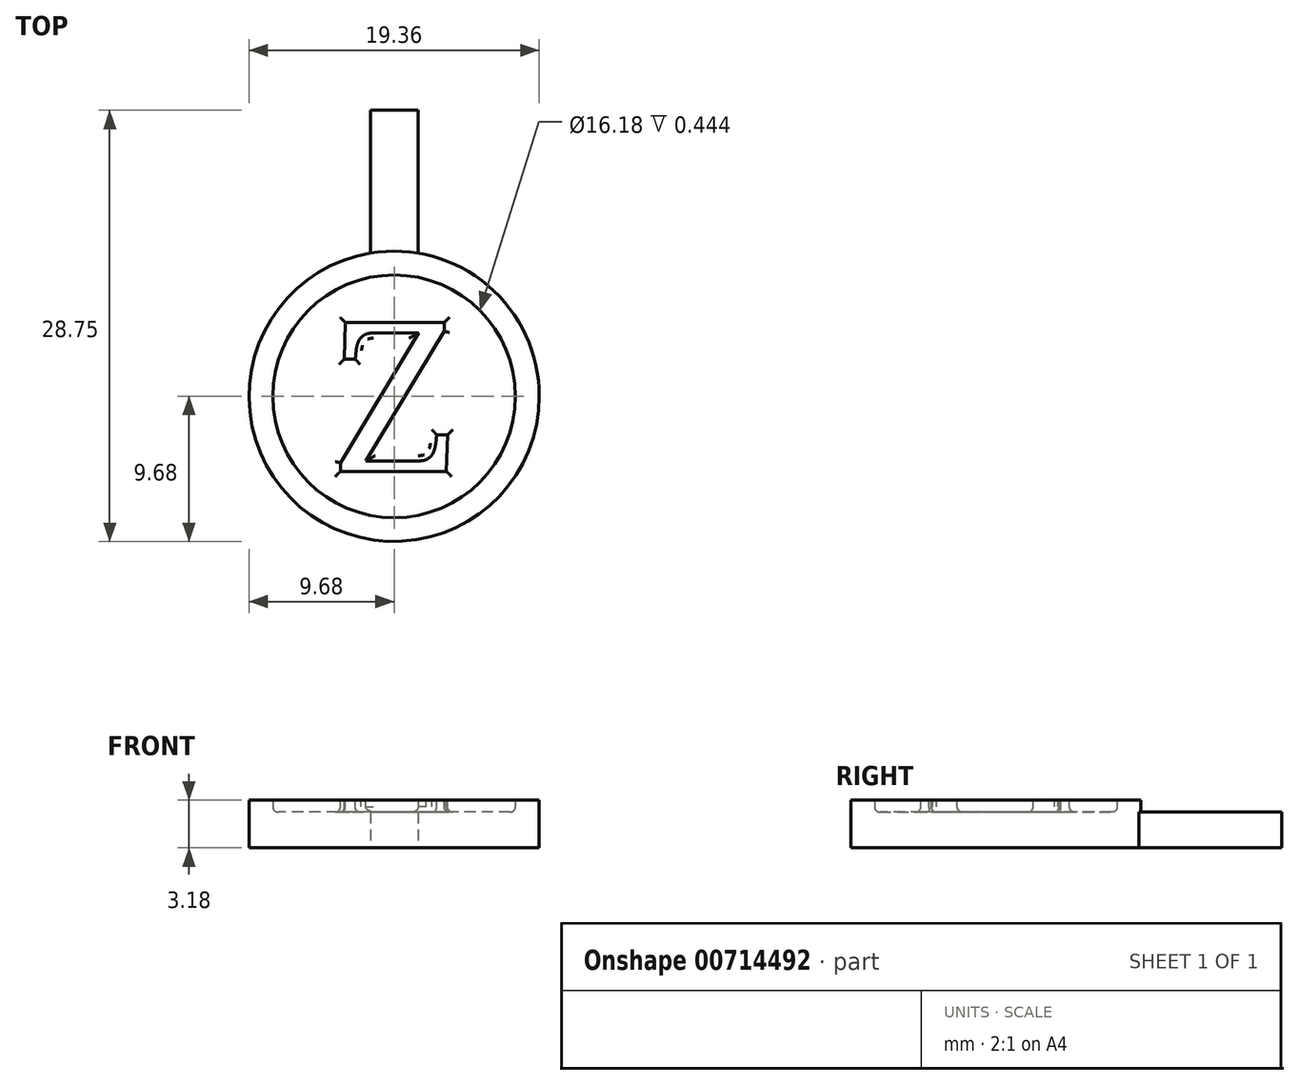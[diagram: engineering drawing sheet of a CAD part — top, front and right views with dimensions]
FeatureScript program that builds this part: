
annotation { "Feature Type Name" : "Feature", "Feature Type Description" : "" }
export const myFeature = defineFeature(function(context is Context, id is Id, definition is map)
    precondition{}
    {
        {
            var Q0;
            Q0=qCreatedBy(makeId("Top.planeOp"),FACE);
            var sketch = newSketch(context, id + "F0", { "sketchPlane" : qUnion([Q0])});
            skCircle(sketch, "E0", {"center": v(0, 0) * mm, "radius": 9.68 * mm});
            skSolve(sketch);
        }
        {
            var Q0;
            Q0=qSketchRegion(id+"F0",true);
            extrude(context, id + "F1", {"entities" : qUnion([Q0]), "depth" : 2.38 * mm, "offsetDistance" : 25.4 * mm});
        }
        {
            var Q0;
            Q0=makeQuery(id+"F1.opExtrude","CAP_FACE",FACE,{"disambiguationData":[OSD([sQuery(id+"F0.wireOp",EDGE,"E0")])],"isStart":false});
            var sketch = newSketch(context, id + "F2", { "sketchPlane" : qUnion([Q0])});
            skCircle(sketch, "E1.0.0", {"center": v(0, 0) * mm, "radius": 9.68 * mm});
            skCircle(sketch, "E2.0", {"center": v(0, 0) * mm, "radius": 8.09 * mm});
            skSolve(sketch);
        }
        {
            var Q0;
            Q0=makeQuery(id+"F2.imprint","IMPRINT",FACE,{"disambiguationData":[TD([[makeQuery(id+"F2.imprint","IMPRINT",EDGE,{"derivedFrom":sQuery(id+"F2.wireOp",EDGE,"E1.0.0")}),1.0]])]});
            extrude(context, id + "F3", {"entities" : qUnion([Q0]), "operationType" : NewBodyOperationType.ADD, "depth" : 0.8 * mm, "offsetDistance" : 25.4 * mm});
        }
        {
            var Q0;
            Q0=qCreatedBy(makeId("Top.planeOp"),FACE);
            var sketch = newSketch(context, id + "F4", { "sketchPlane" : qUnion([Q0])});
            skLineSegment(sketch, "E3.bottom", {"start": v(1.59, 9.55) * mm, "end": v(-1.59, 9.55) * mm});
            skLineSegment(sketch, "E3.top", {"start": v(1.59, 19.07) * mm, "end": v(-1.59, 19.07) * mm});
            skLineSegment(sketch, "E3.left", {"start": v(1.59, 9.55) * mm, "end": v(1.59, 19.07) * mm});
            skLineSegment(sketch, "E3.right", {"start": v(-1.59, 9.55) * mm, "end": v(-1.59, 19.07) * mm});
            skPoint(sketch, "E3.middle", {"position": v(0, 14.3) * mm});
            skSolve(sketch);
        }
        {
            var Q0;
            Q0=qSketchRegion(id+"F4",true);
            var Q1;
            Q1=makeQuery(id+"F3.opExtrude","CAP_FACE",FACE,{"disambiguationData":[OSD([sQuery(id+"F2.wireOp",EDGE,"E1.0.0"),sQuery(id+"F2.wireOp",EDGE,"E2.0")])],"isStart":false});
            extrude(context, id + "F5", {"entities" : qUnion([Q0]), "operationType" : NewBodyOperationType.ADD, "depth" : 2.38 * mm, "endBoundEntityFace" : qUnion([Q1]), "hasOffset" : true, "offsetDistance" : 1 * mm});
        }
        {
            var Q0;
            Q0=makeQuery(id+"F3.opExtrude","CAP_FACE",FACE,{"disambiguationData":[OSD([sQuery(id+"F2.wireOp",EDGE,"E1.0.0"),sQuery(id+"F2.wireOp",EDGE,"E2.0")])],"isStart":false});
            var sketch = newSketch(context, id + "F6", { "sketchPlane" : qUnion([Q0])});
            skPoint(sketch, "E4.middle", {"position": v(0, 0) * mm});
            skText(sketch, "E5", { "text": "Z", "fontName": "NotoSerif-Regular.ttf"});
            skLineSegment(sketch, "E6", {"start": v(4.46, 0) * mm, "end": v(-4.08, 0) * mm, "construction": true});
            skLineSegment(sketch, "E7", {"start": v(0, 8.09) * mm, "end": v(0, -8.09) * mm, "construction": true});
            skLineSegment(sketch, "E8", {"start": v(-8.09, 0) * mm, "end": v(8.09, 0) * mm, "construction": true});
            const initialGuessF6  = {"E5": [-0.00408, -0.005, 1, 0, 0.01]};
            skSetInitialGuess(sketch, initialGuessF6);
            skSolve(sketch);
        }
        {
            var Q0;
            Q0=makeQuery(id+"F6.imprint","IMPRINT",FACE,{"disambiguationData":[TD([[makeQuery(id+"F6.imprint","IMPRINT",EDGE,{"derivedFrom":sQuery(id+"F6.wireOp",EDGE,"E5.sketch_text.stroke-0")}),-1.0]])]});
            var Q1;
            Q1=makeQuery(id+"F1.opExtrude","CAP_FACE",FACE,{"disambiguationData":[OSD([sQuery(id+"F0.wireOp",EDGE,"E0")])],"isStart":false});
            extrude(context, id + "F7", {"entities" : qUnion([Q0]), "operationType" : NewBodyOperationType.ADD, "endBound" : BoundingType.UP_TO_SURFACE, "oppositeDirection" : true, "depth" : 25 * mm, "endBoundEntityFace" : qUnion([Q1]), "offsetDistance" : 25 * mm});
        }
        {
            var Q0;
            Q0=makeQuery(id+"F1.opExtrude","CAP_FACE",FACE,{"disambiguationData":[OSD([sQuery(id+"F0.wireOp",EDGE,"E0")])],"isStart":false});
            fillet(context, id + "F8", {"entities" : qUnion([Q0]), "radius" : .35 * mm, "tangentPropagation" : true, "allowEdgeOverflow" : false});
        }
    });
